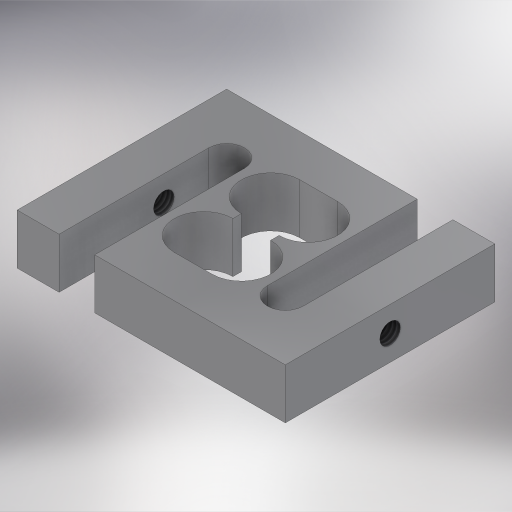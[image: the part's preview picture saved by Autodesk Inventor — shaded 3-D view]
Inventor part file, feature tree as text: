
AUTODESK INVENTOR PART (.ipt)
format: ipt  version: 2023 (Build 270158000, 158)  size: 387,072 bytes
history: native  units: mm
features: sketch x4, extrude x2, hole x2, other x1
ambient origin geometry x8: Origin, YZ Plane, XZ Plane, XY Plane, X Axis, Y Axis, Z Axis, Center Point
bodies: Body1 (feature_tree)
feature tree (9):
  other  "Sólido1"
  extrude  "Extrusão1"  Depth=10.0mm
  hole  "Furo1"  [1 undecoded]
  hole  "Furo2"  [1 undecoded]
  extrude  "Extrusion2"  Depth=50.0mm
  sketch  "Esboço1"  dims[d0=64.0mm d1=10.0mm]
  sketch  "Esboço2"  dims[d2=40.0mm d3=50.0mm]
  sketch  "Esboço3"  dims[d4=8.5mm d5=4.25mm]
  sketch  "Sketch4"  dims[d6=12.0mm d7=0.0mm d8=50.0mm d9=12.0mm d10=6.0mm d11=25.0mm d12=4.917mm d13=12.0mm d14=8.0mm d15=5.0mm d16=90.0deg d17=0.5mm d18=20.594885mm d19=50.0mm d20=12.0mm d21=4.917mm d22=12.0mm d23=4.0mm d24=2.0mm d25=90.0deg d26=8.0mm d27=20.594885mm d28=0.0mm d29=0.0mm d30=23.0mm d31=13.5mm d32=27.0mm d33=0.0mm d34=7.0mm d35=0.0mm d36=0.0mm d37=0.0mm]
note: 2 required parameter values undecoded (feature->parameter linkage not recoverable at this tier; creation-order binding heuristic only, values carry confidence <= 0.55)
